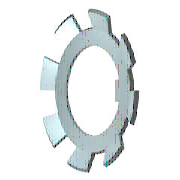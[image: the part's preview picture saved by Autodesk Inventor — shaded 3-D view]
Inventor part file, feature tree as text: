
AUTODESK INVENTOR PART (.ipt)
format: ipt  version: 2021 (Build 250183000, 183)  size: 242,688 bytes
history: native  units: mm (DEFAULTED — no unit token found)
features: sketch x2, extrude x2, pattern_circular x1, other x1, plane x1
ambient origin geometry x8: Origin, YZ Plane, XZ Plane, XY Plane, X Axis, Y Axis, Z Axis, Center Point
bodies: Solid1 (feature_tree), Body (feature_tree)
feature tree (7):
  sketch  "Sketch2"  dims[d3=193.0mm d4=222.0mm d5=4.363323mm d6=2.5mm d7=90.0deg d8=165.0mm d9=18.0mm d10=75.0mm d16=0.826735mm d17=2.5mm d18=0.0mm d19=2.5mm d20=0.0mm d21=190.0mm d23=360.0deg d24=0.0mm d25=0.0mm d26=90.0deg d27=0.0mm]
  extrude  "Cut"  Depth=2.5mm
  extrude  "Nib"  Depth=2.5mm
  pattern_circular  "Cuts"  [2 undecoded]
  other  "Work Axis1"
  plane  "Work Plane1"
  sketch  "Sketch1"  dims[d1=2.5mm d2=165.0mm]
note: 2 required parameter values undecoded (feature->parameter linkage not recoverable at this tier; creation-order binding heuristic only, values carry confidence <= 0.55)
